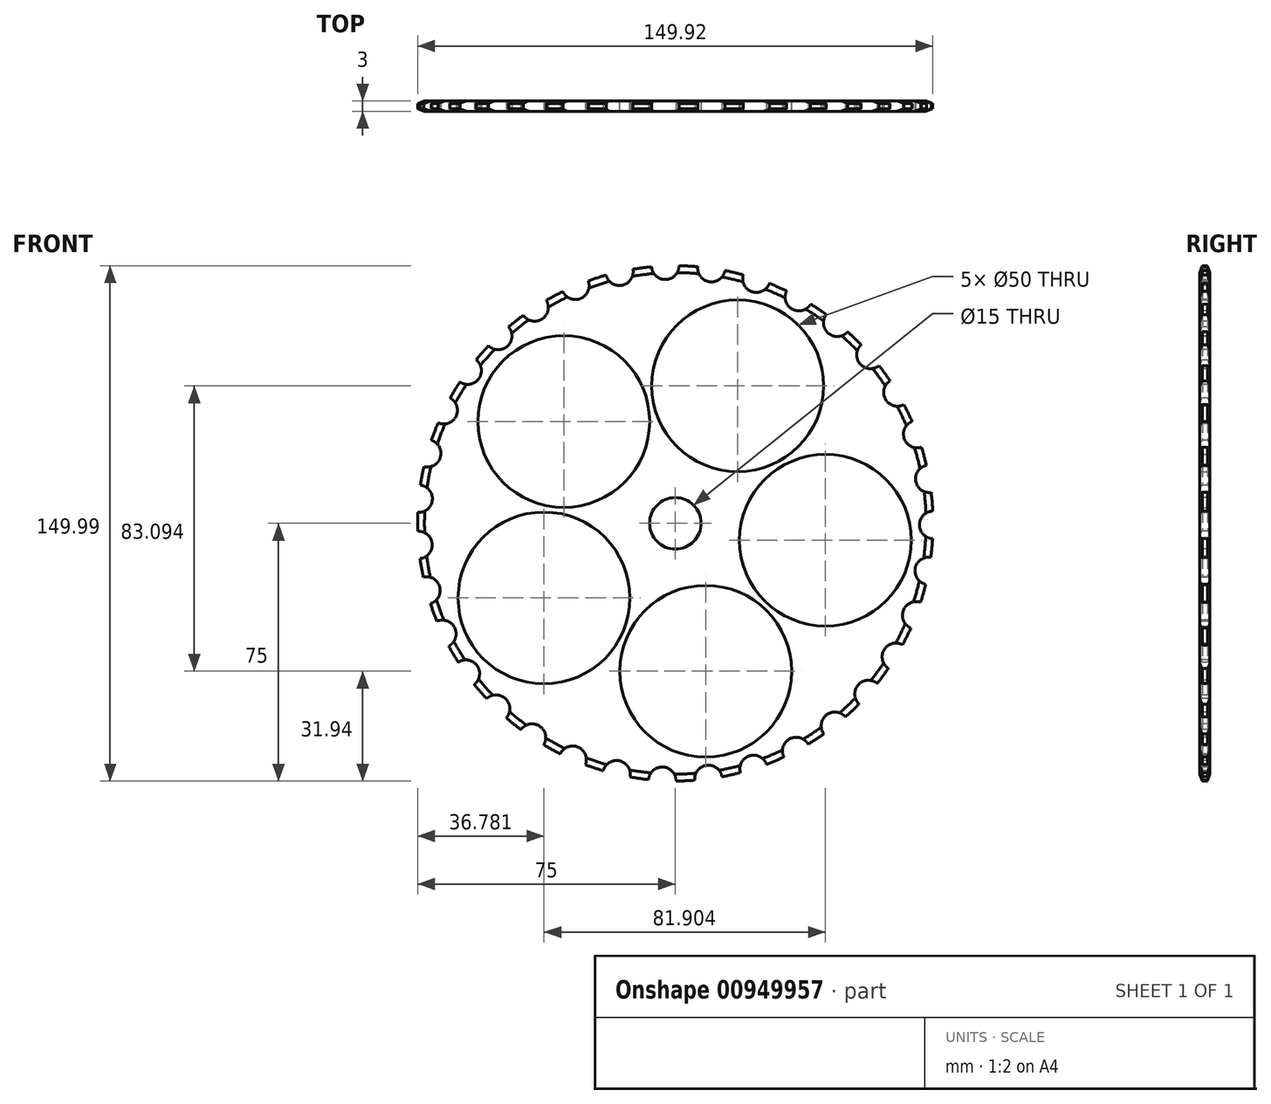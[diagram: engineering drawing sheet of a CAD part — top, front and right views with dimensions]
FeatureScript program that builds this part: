
annotation { "Feature Type Name" : "Feature", "Feature Type Description" : "" }
export const myFeature = defineFeature(function(context is Context, id is Id, definition is map)
    precondition{}
    {
        {
            var Q0;
            Q0=qCreatedBy(makeId("Front.planeOp"),FACE);
            var sketch = newSketch(context, id + "F0", { "sketchPlane" : qUnion([Q0])});
            skCircle(sketch, "E0", {"center": v(0, 0) * mm, "radius": 75 * mm});
            skCircle(sketch, "E1", {"center": v(-32.46, 29.64) * mm, "radius": 25 * mm});
            skCircle(sketch, "E2.1.0", {"center": v(-38.22, -21.72) * mm, "radius": 25 * mm});
            skCircle(sketch, "E2.2.0", {"center": v(8.84, -43.06) * mm, "radius": 25 * mm});
            skCircle(sketch, "E2.3.0", {"center": v(43.68, -4.9) * mm, "radius": 25 * mm});
            skCircle(sketch, "E2.4.0", {"center": v(18.16, 40.03) * mm, "radius": 25 * mm});
            skSolve(sketch);
        }
        {
            var Q0;
            Q0=makeQuery(id+"F0.imprint","IMPRINT",FACE,{"disambiguationData":[TD([[makeQuery(id+"F0.imprint","IMPRINT",EDGE,{"derivedFrom":sQuery(id+"F0.wireOp",EDGE,"E0")}),1.0]])]});
            extrude(context, id + "F1", {"entities" : qUnion([Q0]), "depth" : 3 * mm, "offsetDistance" : 25 * mm});
        }
        {
            var Q0;
            {var subQ0=sQuery(id+"F0.wireOp",EDGE,"E0");Q0=makeQuery(id+"FjPS6zSCau8WYdw_1.boolean.opBoolean","SPLIT",EDGE,{"disambiguationData":[TD([makeQuery(id+"F1.opExtrude","SWEPT_FACE",FACE,{"disambiguationData":[OSD([subQ0])]}),makeQuery(id+"F1.opExtrude","CAP_FACE",FACE,{"disambiguationData":[OSD([subQ0])],"isStart":false}),makeQuery(id+"FjPS6zSCau8WYdw_1.opExtrude","SWEPT_FACE",FACE,{"disambiguationData":[OSD([sQuery(id+"F4.wireOp",EDGE,"E4.5.0")])]}),makeQuery(id+"FjPS6zSCau8WYdw_1.opExtrude","SWEPT_FACE",FACE,{"disambiguationData":[OSD([sQuery(id+"F4.wireOp",EDGE,"E4.6.0")])]})])],"derivedFrom":makeQuery(id+"F1.opExtrude","CAP_EDGE",EDGE,{"disambiguationData":[OSD([subQ0])],"isStart":false})});}
            chamfer(context, id + "F2", {"entities" : qUnion([Q0]), "chamferType" : ChamferType.TWO_OFFSETS, "width1" : 2 * mm, "oppositeDirection" : false, "width2" : 0.75 * mm, "tangentPropagation" : true});
        }
        {
            var Q0;
            {var subQ0=sQuery(id+"F0.wireOp",EDGE,"E0");Q0=makeQuery(id+"FjPS6zSCau8WYdw_1.boolean.opBoolean","SPLIT",EDGE,{"disambiguationData":[TD([makeQuery(id+"F1.opExtrude","SWEPT_FACE",FACE,{"disambiguationData":[OSD([subQ0])]}),makeQuery(id+"F1.opExtrude","CAP_FACE",FACE,{"disambiguationData":[OSD([subQ0])],"isStart":true}),makeQuery(id+"FjPS6zSCau8WYdw_1.opExtrude","SWEPT_FACE",FACE,{"disambiguationData":[OSD([sQuery(id+"F4.wireOp",EDGE,"E4.21.0")])]}),makeQuery(id+"FjPS6zSCau8WYdw_1.opExtrude","SWEPT_FACE",FACE,{"disambiguationData":[OSD([sQuery(id+"F4.wireOp",EDGE,"E4.22.0")])]})])],"derivedFrom":makeQuery(id+"F1.opExtrude","CAP_EDGE",EDGE,{"disambiguationData":[OSD([subQ0])],"isStart":true})});}
            chamfer(context, id + "F3", {"entities" : qUnion([Q0]), "chamferType" : ChamferType.TWO_OFFSETS, "width1" : 0.75 * mm, "oppositeDirection" : false, "width2" : 2 * mm, "tangentPropagation" : true});
        }
        {
            var Q0;
            Q0=makeQuery(id+"F1.opExtrude","CAP_FACE",FACE,{"disambiguationData":[OSD([sQuery(id+"F0.wireOp",EDGE,"E0")])],"isStart":false});
            var sketch = newSketch(context, id + "F4", { "sketchPlane" : qUnion([Q0])});
            skCircle(sketch, "E3", {"center": v(-67.41, 32.95) * mm, "radius": 4 * mm});
            skCircle(sketch, "E4.1.0", {"center": v(-72.21, 20.38) * mm, "radius": 4 * mm});
            skCircle(sketch, "E4.2.0", {"center": v(-74.7, 7.16) * mm, "radius": 4 * mm});
            skCircle(sketch, "E4.3.0", {"center": v(-74.77, -6.3) * mm, "radius": 4 * mm});
            skCircle(sketch, "E4.4.0", {"center": v(-72.44, -19.54) * mm, "radius": 4 * mm});
            skCircle(sketch, "E4.5.0", {"center": v(-67.79, -32.16) * mm, "radius": 4 * mm});
            skCircle(sketch, "E4.6.0", {"center": v(-60.96, -43.75) * mm, "radius": 4 * mm});
            skCircle(sketch, "E4.7.0", {"center": v(-52.17, -53.93) * mm, "radius": 4 * mm});
            skCircle(sketch, "E4.8.0", {"center": v(-41.7, -62.38) * mm, "radius": 4 * mm});
            skCircle(sketch, "E4.9.0", {"center": v(-29.89, -68.82) * mm, "radius": 4 * mm});
            skCircle(sketch, "E4.10.0", {"center": v(-17.12, -73.05) * mm, "radius": 4 * mm});
            skCircle(sketch, "E4.11.0", {"center": v(-3.8, -74.94) * mm, "radius": 4 * mm});
            skCircle(sketch, "E4.12.0", {"center": v(9.64, -74.41) * mm, "radius": 4 * mm});
            skCircle(sketch, "E4.13.0", {"center": v(22.77, -71.5) * mm, "radius": 4 * mm});
            skCircle(sketch, "E4.14.0", {"center": v(35.17, -66.28) * mm, "radius": 4 * mm});
            skCircle(sketch, "E4.15.0", {"center": v(46.44, -58.93) * mm, "radius": 4 * mm});
            skCircle(sketch, "E4.16.0", {"center": v(56.22, -49.7) * mm, "radius": 4 * mm});
            skCircle(sketch, "E4.17.0", {"center": v(64.19, -38.86) * mm, "radius": 4 * mm});
            skCircle(sketch, "E4.18.0", {"center": v(70.1, -26.77) * mm, "radius": 4 * mm});
            skCircle(sketch, "E4.19.0", {"center": v(73.75, -13.83) * mm, "radius": 4 * mm});
            skCircle(sketch, "E4.20.0", {"center": v(75.03, -0.44) * mm, "radius": 4 * mm});
            skCircle(sketch, "E4.21.0", {"center": v(73.9, 12.97) * mm, "radius": 4 * mm});
            skCircle(sketch, "E4.22.0", {"center": v(70.4, 25.96) * mm, "radius": 4 * mm});
            skCircle(sketch, "E4.23.0", {"center": v(64.63, 38.1) * mm, "radius": 4 * mm});
            skCircle(sketch, "E4.24.0", {"center": v(56.8, 49.04) * mm, "radius": 4 * mm});
            skCircle(sketch, "E4.25.0", {"center": v(47.12, 58.4) * mm, "radius": 4 * mm});
            skCircle(sketch, "E4.26.0", {"center": v(35.94, 65.87) * mm, "radius": 4 * mm});
            skCircle(sketch, "E4.27.0", {"center": v(23.6, 71.22) * mm, "radius": 4 * mm});
            skCircle(sketch, "E4.28.0", {"center": v(10.5, 74.3) * mm, "radius": 4 * mm});
            skCircle(sketch, "E4.29.0", {"center": v(-2.93, 74.98) * mm, "radius": 4 * mm});
            skCircle(sketch, "E4.30.0", {"center": v(-16.27, 73.25) * mm, "radius": 4 * mm});
            skCircle(sketch, "E4.31.0", {"center": v(-29.09, 69.16) * mm, "radius": 4 * mm});
            skCircle(sketch, "E4.32.0", {"center": v(-40.97, 62.86) * mm, "radius": 4 * mm});
            skCircle(sketch, "E4.33.0", {"center": v(-51.54, 54.53) * mm, "radius": 4 * mm});
            skCircle(sketch, "E4.34.0", {"center": v(-60.45, 44.45) * mm, "radius": 4 * mm});
            skPoint(sketch, "E4.center", {"position": v(0, 0) * mm});
            skCircle(sketch, "E5", {"center": v(0, 0) * mm, "radius": 7.5 * mm});
            skCircle(sketch, "E6", {"center": v(0, 0) * mm, "radius": 24.55 * mm, "construction": true});
            skCircle(sketch, "E7", {"center": v(0, 0) * mm, "radius": 106.64 * mm, "construction": true});
            skLineSegment(sketch, "E8", {"start": v(0, 115.3) * mm, "end": v(0, -115.73) * mm, "construction": true});
            skLineSegment(sketch, "E9", {"start": v(-114.53, 0) * mm, "end": v(114.1, 0) * mm, "construction": true});
            skLineSegment(sketch, "E10.1.0", {"start": v(-80.99, -80.99) * mm, "end": v(80.68, 80.68) * mm, "construction": true});
            skLineSegment(sketch, "E10.2.0", {"start": v(0, -114.53) * mm, "end": v(0, 114.1) * mm, "construction": true});
            skLineSegment(sketch, "E10.3.0", {"start": v(80.99, -80.99) * mm, "end": v(-80.68, 80.68) * mm, "construction": true});
            skLineSegment(sketch, "E10.4.0", {"start": v(-29.05, 0) * mm, "end": v(-78.54, 0) * mm, "construction": true});
            skLineSegment(sketch, "E10.5.0", {"start": v(80.99, 80.99) * mm, "end": v(-80.68, -80.68) * mm, "construction": true});
            skLineSegment(sketch, "E10.6.0", {"start": v(0, 114.53) * mm, "end": v(0, -114.1) * mm, "construction": true});
            skLineSegment(sketch, "E10.7.0", {"start": v(-56.1, 56.1) * mm, "end": v(-20.44, 20.44) * mm, "construction": true});
            skLineSegment(sketch, "E11", {"start": v(-59.84, 59.84) * mm, "end": v(-17.36, 17.36) * mm});
            skLineSegment(sketch, "E12", {"start": v(-24.55, 0) * mm, "end": v(-83.68, 0) * mm});
            skPoint(sketch, "E13.1.internal.snap0", {"position": v(-20.96, 8.68) * mm});
            skPoint(sketch, "E14.newPointB", {"position": v(-80.99, 80.99) * mm});
            skPoint(sketch, "E15.newPointB", {"position": v(-114.1, 0) * mm});
            skPoint(sketch, "E16.newPointB", {"position": v(114.53, 0) * mm});
            skPoint(sketch, "E17.newPointB", {"position": v(80.68, -80.68) * mm});
            skLineSegment(sketch, "E18.1.0", {"start": v(-20.53, -76.62) * mm, "end": v(-7.48, -27.92) * mm, "construction": true});
            skLineSegment(sketch, "E18.2.0", {"start": v(76.62, 20.53) * mm, "end": v(27.92, 7.48) * mm, "construction": true});
            skSolve(sketch);
        }
        {
            var Q0;
            Q0=qSketchRegion(id+"F4",true);
            extrude(context, id + "F5", {"entities" : qUnion([Q0]), "operationType" : NewBodyOperationType.REMOVE, "endBound" : BoundingType.THROUGH_ALL, "oppositeDirection" : true, "depth" : 25 * mm, "offsetDistance" : 25 * mm});
        }
    });
